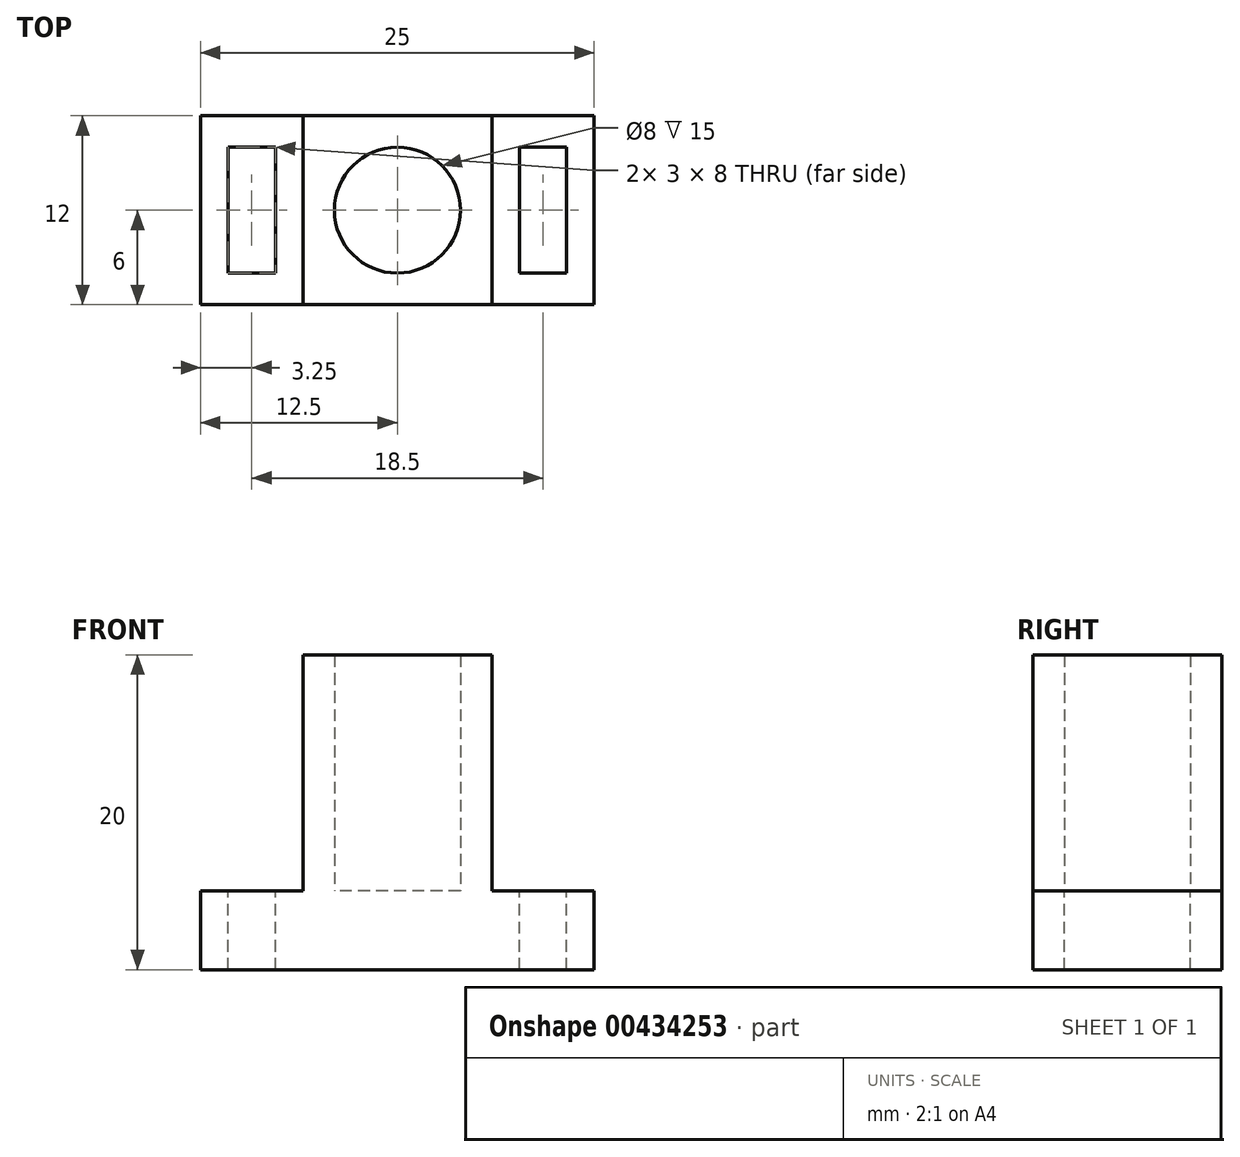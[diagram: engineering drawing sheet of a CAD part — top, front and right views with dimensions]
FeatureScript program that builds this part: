
annotation { "Feature Type Name" : "Feature", "Feature Type Description" : "" }
export const myFeature = defineFeature(function(context is Context, id is Id, definition is map)
    precondition{}
    {
        {
            var Q0;
            Q0=qCreatedBy(makeId("Top.planeOp"),FACE);
            var sketch = newSketch(context, id + "F0", { "sketchPlane" : qUnion([Q0])});
            skCircle(sketch, "E0", {"center": v(0, 0) * mm, "radius": 4 * mm});
            skLineSegment(sketch, "E1.bottom", {"start": v(6, -6) * mm, "end": v(-6, -6) * mm});
            skLineSegment(sketch, "E1.top", {"start": v(6, 6) * mm, "end": v(-6, 6) * mm});
            skLineSegment(sketch, "E1.left", {"start": v(6, -6) * mm, "end": v(6, 6) * mm});
            skLineSegment(sketch, "E1.right", {"start": v(-6, -6) * mm, "end": v(-6, 6) * mm});
            skSolve(sketch);
        }
        {
            var Q0;
            Q0 = qSketchRegion(id + "F0", true);
            extrude(context, id + "F1", {"entities" : qUnion([Q0]), "depth" : 15 * mm});
        }
        {
            var Q0;
            Q0=makeQuery(id+"F1.opExtrude","CAP_FACE",FACE,{"disambiguationData":[OSD([sQuery(id+"F0.wireOp",EDGE,"E0"),sQuery(id+"F0.wireOp",EDGE,"E1.bottom"),sQuery(id+"F0.wireOp",EDGE,"E1.top"),sQuery(id+"F0.wireOp",EDGE,"E1.left"),sQuery(id+"F0.wireOp",EDGE,"E1.right")])],"isStart":true});
            var sketch = newSketch(context, id + "F2", { "sketchPlane" : qUnion([Q0])});
            skLineSegment(sketch, "E2.bottom", {"start": v(-12.5, 6) * mm, "end": v(12.5, 6) * mm});
            skLineSegment(sketch, "E2.top", {"start": v(-12.5, -6) * mm, "end": v(12.5, -6) * mm});
            skLineSegment(sketch, "E2.left", {"start": v(-12.5, 6) * mm, "end": v(-12.5, -6) * mm});
            skLineSegment(sketch, "E2.right", {"start": v(12.5, 6) * mm, "end": v(12.5, -6) * mm});
            skPoint(sketch, "E2.middle", {"position": v(0, 0) * mm});
            skSolve(sketch);
        }
        {
            var Q0;
            Q0 = qSketchRegion(id + "F2", true);
            extrude(context, id + "F3", {"entities" : qUnion([Q0]), "operationType" : NewBodyOperationType.ADD, "depth" : 5 * mm});
        }
        {
            var Q0;
            {var subQ0=sQuery(id+"F2.wireOp",EDGE,"E2.top");var subQ1=sQuery(id+"F2.wireOp",EDGE,"E2.bottom");var subQ2=sQuery(id+"F2.wireOp",EDGE,"E2.left");Q0=makeQuery(id+"F3.boolean.opBoolean","SPLIT",FACE,{"disambiguationData":[TD([makeQuery(id+"F1.opExtrude","SWEPT_FACE",FACE,{"disambiguationData":[OSD([sQuery(id+"F0.wireOp",EDGE,"E1.right")])]})])],"derivedFrom":makeQuery(id+"F3.opExtrude","CAP_FACE",FACE,{"disambiguationData":[OSD([subQ1,subQ0,subQ2,sQuery(id+"F2.wireOp",EDGE,"E2.right")])],"isStart":true})});}
            var sketch = newSketch(context, id + "F4", { "sketchPlane" : qUnion([Q0])});
            skLineSegment(sketch, "E3.bottom", {"start": v(-7.75, -4) * mm, "end": v(-10.75, -4) * mm});
            skLineSegment(sketch, "E3.top", {"start": v(-7.75, 4) * mm, "end": v(-10.75, 4) * mm});
            skLineSegment(sketch, "E3.left", {"start": v(-7.75, -4) * mm, "end": v(-7.75, 4) * mm});
            skLineSegment(sketch, "E3.right", {"start": v(-10.75, -4) * mm, "end": v(-10.75, 4) * mm});
            skPoint(sketch, "E3.middle", {"position": v(-9.25, 0) * mm});
            skPoint(sketch, "E3.middle.positionSnap0", {"position": v(-9.25, -6) * mm});
            skPoint(sketch, "E3.middle.positionSnap1", {"position": v(-12.5, 0) * mm});
            skPoint(sketch, "E3.centerSnap0", {"position": v(-9.25, -6) * mm});
            skPoint(sketch, "E3.centerSnap1", {"position": v(-12.5, 0) * mm});
            skLineSegment(sketch, "E4", {"start": v(0, 0) * mm, "end": v(0, 9.69) * mm, "construction": true});
            skLineSegment(sketch, "E5.MirrorCS", {"start": v(7.75, -4) * mm, "end": v(7.75, 4) * mm});
            skLineSegment(sketch, "E6.MirrorCS", {"start": v(7.75, 4) * mm, "end": v(10.75, 4) * mm});
            skLineSegment(sketch, "E7.MirrorCS", {"start": v(10.75, -4) * mm, "end": v(10.75, 4) * mm});
            skLineSegment(sketch, "E8.MirrorCS", {"start": v(7.75, -4) * mm, "end": v(10.75, -4) * mm});
            skSolve(sketch);
        }
        {
            var Q0;
            Q0 = qSketchRegion(id + "F4", true);
            extrude(context, id + "F5", {"entities" : qUnion([Q0]), "operationType" : NewBodyOperationType.REMOVE, "oppositeDirection" : true, "depth" : 5 * mm});
        }
    });
